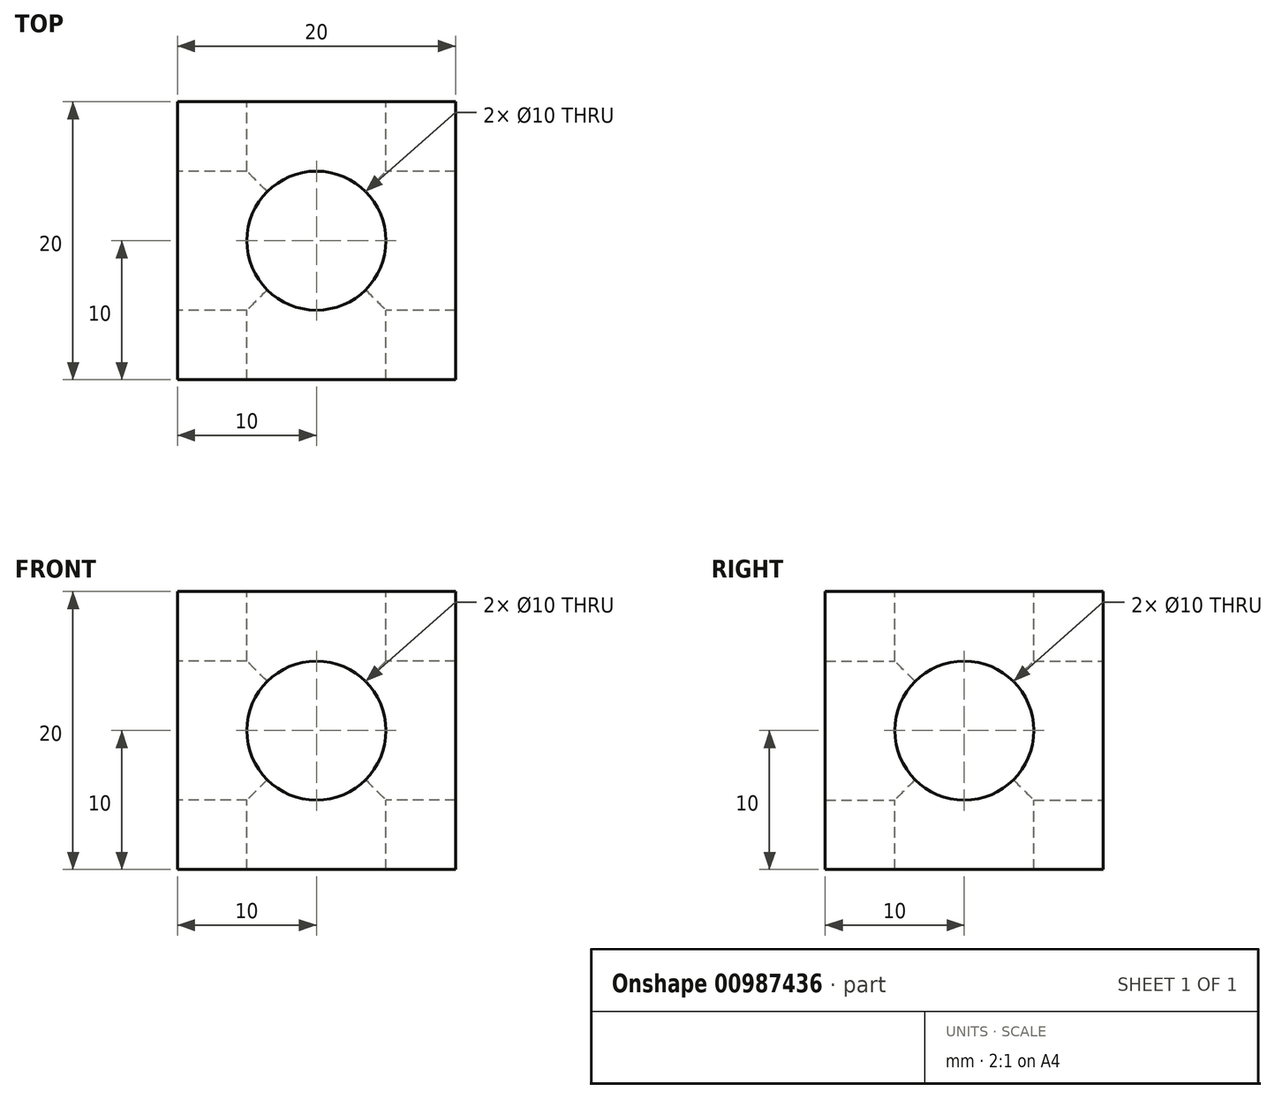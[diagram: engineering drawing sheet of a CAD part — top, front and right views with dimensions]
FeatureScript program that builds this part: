
annotation { "Feature Type Name" : "Feature", "Feature Type Description" : "" }
export const myFeature = defineFeature(function(context is Context, id is Id, definition is map)
    precondition{}
    {
        {
            var Q0;
            Q0=qCreatedBy(makeId("Front.planeOp"),FACE);
            var sketch = newSketch(context, id + "F0", { "sketchPlane" : qUnion([Q0])});
            skLineSegment(sketch, "E0", {"start": v(0, 20) * mm, "end": v(20, 20) * mm});
            skLineSegment(sketch, "E1", {"start": v(20, 20) * mm, "end": v(20, 0) * mm});
            skLineSegment(sketch, "E2", {"start": v(0, 20) * mm, "end": v(0, 0) * mm});
            skLineSegment(sketch, "E3", {"start": v(0, 0) * mm, "end": v(20, 0) * mm});
            skSolve(sketch);
        }
        {
            var Q0;
            Q0=makeQuery(id+"F0.imprint","IMPRINT",FACE,{"disambiguationData":[TD([[makeQuery(id+"F0.imprint","IMPRINT",EDGE,{"derivedFrom":sQuery(id+"F0.wireOp",EDGE,"E0")}),-1.0]])]});
            extrude(context, id + "F1", {"entities" : qUnion([Q0]), "depth" : 20 * mm, "offsetDistance" : 25 * mm});
        }
        {
            var Q0;
            Q0=qCreatedBy(makeId("Top.planeOp"),FACE);
            var sketch = newSketch(context, id + "F2", { "sketchPlane" : qUnion([Q0])});
            skCircle(sketch, "E4", {"center": v(10, -10) * mm, "radius": 5 * mm});
            skSolve(sketch);
        }
        {
            var Q0;
            Q0=sQuery(id+"F2.wireOp",VERTEX,"E4.center");
            var Q1;
            Q1=makeQuery(id+"F1.opExtrude","SWEPT_BODY",BODY,{"disambiguationData":[OSD([sQuery(id+"F0.wireOp",EDGE,"E0"),sQuery(id+"F0.wireOp",EDGE,"E1"),sQuery(id+"F0.wireOp",EDGE,"E2"),sQuery(id+"F0.wireOp",EDGE,"E3")])]});
            hole(context, id + "F3", {"style" : HoleStyle.SIMPLE, "endStyle" : HoleEndStyle.THROUGH, "oppositeDirection" : true, "holeDiameter" : 10 * mm, "majorDiameter" : 5 * mm, "isTappedThrough" : true, "tappedDepth" : 12 * mm, "tapClearance" : 3, "locations" : qUnion([Q0]), "scope" : qUnion([Q1]), "startStyle" : HoleStartStyle.PART});
        }
        {
            var Q0;
            Q0=makeQuery(id+"F1.opExtrude","CAP_FACE",FACE,{"disambiguationData":[OSD([sQuery(id+"F0.wireOp",EDGE,"E0"),sQuery(id+"F0.wireOp",EDGE,"E1"),sQuery(id+"F0.wireOp",EDGE,"E2"),sQuery(id+"F0.wireOp",EDGE,"E3")])],"isStart":false});
            var sketch = newSketch(context, id + "F4", { "sketchPlane" : qUnion([Q0])});
            skCircle(sketch, "E5", {"center": v(10, 10) * mm, "radius": 5 * mm});
            skSolve(sketch);
        }
        {
            var Q0;
            Q0=sQuery(id+"F4.wireOp",VERTEX,"E5.center");
            var Q1;
            Q1=makeQuery(id+"F1.opExtrude","SWEPT_BODY",BODY,{"disambiguationData":[OSD([sQuery(id+"F0.wireOp",EDGE,"E0"),sQuery(id+"F0.wireOp",EDGE,"E1"),sQuery(id+"F0.wireOp",EDGE,"E2"),sQuery(id+"F0.wireOp",EDGE,"E3")])]});
            hole(context, id + "F5", {"style" : HoleStyle.SIMPLE, "endStyle" : HoleEndStyle.THROUGH, "holeDiameter" : 10 * mm, "majorDiameter" : 5 * mm, "isTappedThrough" : true, "tappedDepth" : 12 * mm, "tapClearance" : 3, "locations" : qUnion([Q0]), "scope" : qUnion([Q1]), "startStyle" : HoleStartStyle.PART});
        }
        {
            var Q0;
            Q0=makeQuery(id+"F1.opExtrude","SWEPT_FACE",FACE,{"disambiguationData":[OSD([sQuery(id+"F0.wireOp",EDGE,"E1")])]});
            var sketch = newSketch(context, id + "F6", { "sketchPlane" : qUnion([Q0])});
            skCircle(sketch, "E6", {"center": v(-10, 10) * mm, "radius": 5 * mm});
            skSolve(sketch);
        }
        {
            var Q0;
            Q0=sQuery(id+"F6.wireOp",VERTEX,"E6.center");
            var Q1;
            Q1=makeQuery(id+"F1.opExtrude","SWEPT_BODY",BODY,{"disambiguationData":[OSD([sQuery(id+"F0.wireOp",EDGE,"E0"),sQuery(id+"F0.wireOp",EDGE,"E1"),sQuery(id+"F0.wireOp",EDGE,"E2"),sQuery(id+"F0.wireOp",EDGE,"E3")])]});
            hole(context, id + "F7", {"style" : HoleStyle.SIMPLE, "endStyle" : HoleEndStyle.THROUGH, "holeDiameter" : 10 * mm, "majorDiameter" : 5 * mm, "isTappedThrough" : true, "tappedDepth" : 12 * mm, "tapClearance" : 3, "locations" : qUnion([Q0]), "scope" : qUnion([Q1]), "startStyle" : HoleStartStyle.PART});
        }
    });
